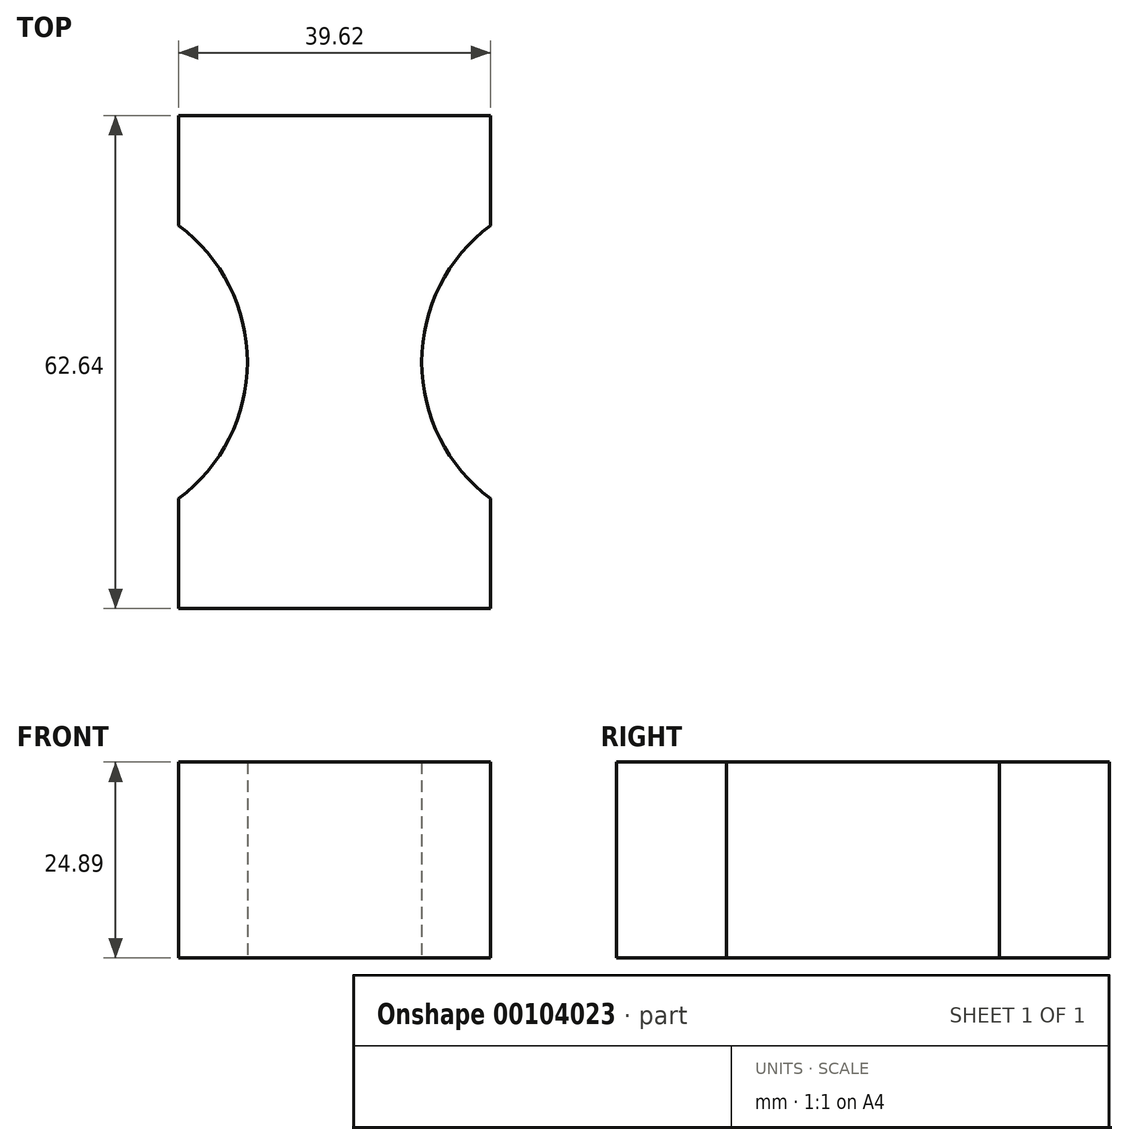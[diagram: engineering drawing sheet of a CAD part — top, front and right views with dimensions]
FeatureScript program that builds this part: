
annotation { "Feature Type Name" : "Feature", "Feature Type Description" : "" }
export const myFeature = defineFeature(function(context is Context, id is Id, definition is map)
    precondition{}
    {
        {
            var Q0;
            Q0=qCreatedBy(makeId("Top.planeOp"),FACE);
            var sketch = newSketch(context, id + "F0", { "sketchPlane" : qUnion([Q0])});
            skLineSegment(sketch, "E0.bottom", {"start": v(-31.88, 35.88) * mm, "end": v(7.74, 35.88) * mm});
            skLineSegment(sketch, "E0.top", {"start": v(-31.88, -26.76) * mm, "end": v(7.74, -26.76) * mm});
            skLineSegment(sketch, "E1", {"start": v(-31.88, 35.88) * mm, "end": v(-31.88, 21.9) * mm});
            skLineSegment(sketch, "E2", {"start": v(-31.88, -26.76) * mm, "end": v(-31.88, -12.79) * mm});
            skArc(sketch, "E3", {"start": v(-31.88, -12.79) * mm, "mid": v(-23.14, 4.56) * mm, "end": v(-31.88, 21.9) * mm});
            skLineSegment(sketch, "E4", {"start": v(7.74, -26.76) * mm, "end": v(7.74, -12.79) * mm});
            skLineSegment(sketch, "E5", {"start": v(7.74, 35.88) * mm, "end": v(7.74, 21.9) * mm});
            skArc(sketch, "E6", {"start": v(7.74, 21.9) * mm, "mid": v(-1, 4.56) * mm, "end": v(7.74, -12.79) * mm});
            skSolve(sketch);
        }
        {
            var Q0;
            Q0 = qSketchRegion(id + "F0", true);
            extrude(context, id + "F1", {"entities" : qUnion([Q0]), "depth" : 24.9 * mm});
        }
        {
            var Q0;
            Q0=makeQuery(id+"F1.opExtrude","SWEPT_FACE",FACE,{"disambiguationData":[OSD([sQuery(id+"F0.wireOp",EDGE,"E0.top")])]});
            var Q1;
            Q1=makeQuery(id+"F1.opExtrude","CAP_VERTEX",VERTEX,{"disambiguationData":[OSD([sQuery(id+"F0.wireOp",EDGE,"E0.top"),sQuery(id+"F0.wireOp",EDGE,"E4")])],"isStart":false});
            cPlane(context, id + "F2", {"entities" : qUnion([Q0, Q1]), "cplaneType" : CPlaneType.PLANE_POINT, "offset" : 152.4 * mm, "width" : 152.4 * mm, "height" : 152.4 * mm});
        }
    });
